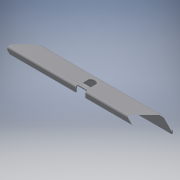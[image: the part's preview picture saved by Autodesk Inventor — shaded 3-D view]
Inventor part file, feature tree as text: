
AUTODESK INVENTOR PART (.ipt)
format: ipt  version: 2016 (Build 200138000, 138)  size: 152,064 bytes
history: native  units: mm
features: sheet_metal_op x7, sketch x5, other x5
ambient origin geometry x8: Origin, YZ Plane, XZ Plane, XY Plane, X Axis, Y Axis, Z Axis, Center Point
bodies: Solid1 (feature_tree)
feature tree (17):
  sheet_metal_op  "Face1"
  sheet_metal_op  "Flange1"
  sheet_metal_op  "Flange2"
  sketch  "Sketch1"  dims[d0=2.0mm]
  other  "Plate1"
  sketch  "Sketch2"  dims[d1=40.0mm]
  other  "Plate2"
  sheet_metal_op  "Bend1"
  sheet_metal_op  "Corner1"
  sketch  "Sketch3"  dims[d2=310.0mm]
  other  "Plate3"
  sheet_metal_op  "Bend2"
  sheet_metal_op  "Corner2"
  sketch  "Sketch4"  dims[d3=2.0mm]
  sketch  "Sketch5"  dims[d4=1.0mm d5=4.0mm d6=2.0mm d7=25.0mm d8=90.0deg d9=2.0mm d10=8.0mm d11=2.0mm d12=2.0mm d13=2.0mm d14=1.0mm d15=4.0mm d16=2.0mm d17=12.0mm d18=90.0deg d19=2.0mm d20=8.0mm d21=2.0mm d22=2.0mm d23=2.0mm d24=0.0mm d25=20.5mm d26=16.5mm d27=20.0mm d28=6.0mm d29=2.0mm d30=0.0mm]
  other  "Cut1"
  other  "Cut2"
